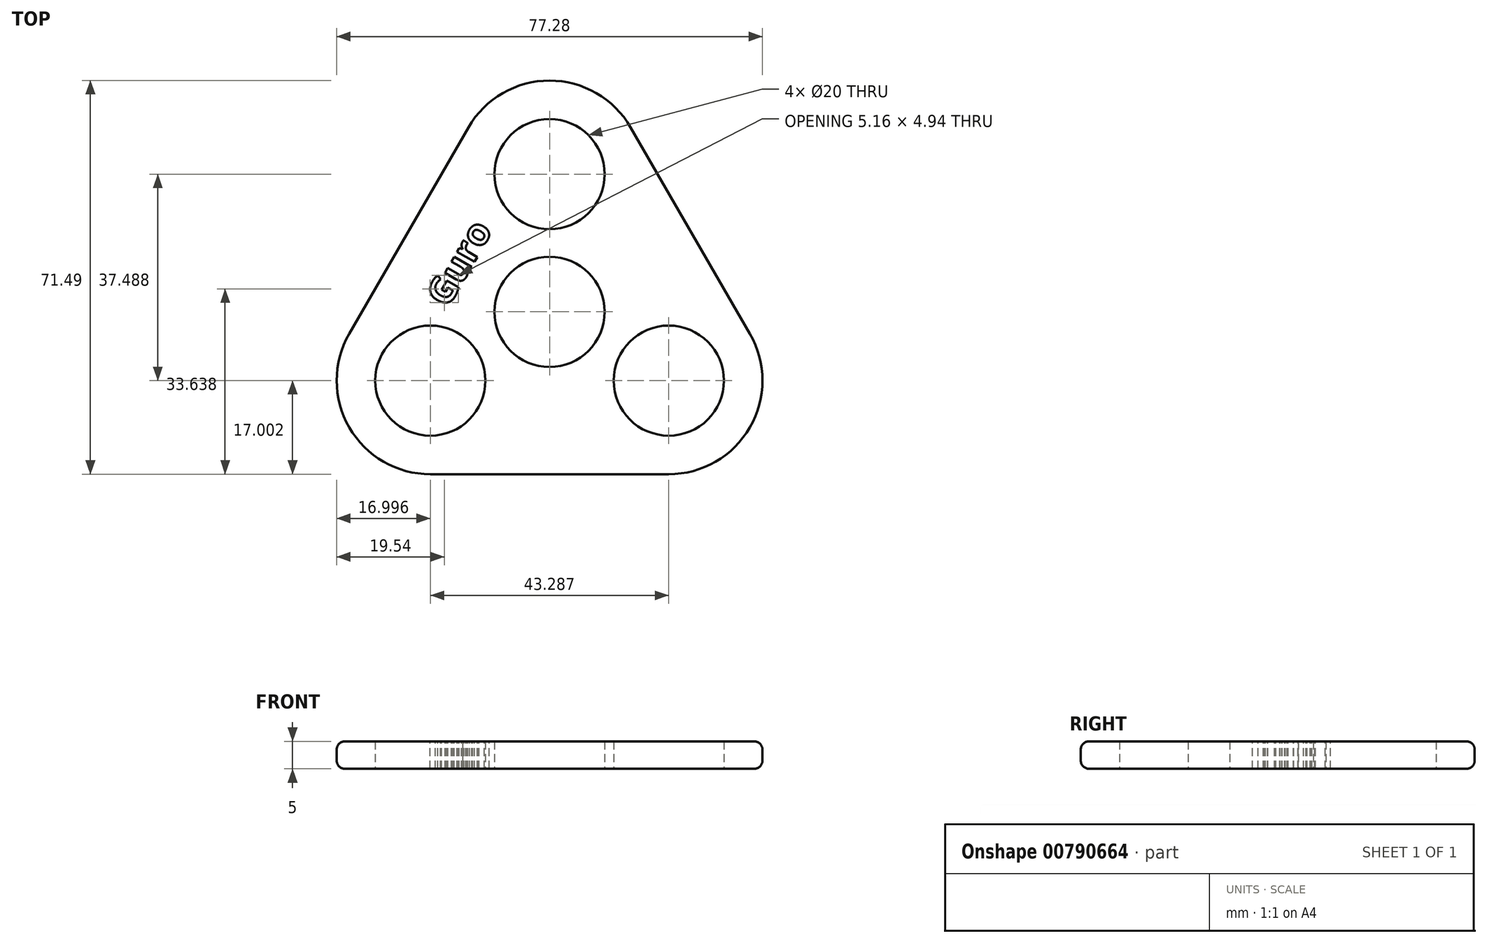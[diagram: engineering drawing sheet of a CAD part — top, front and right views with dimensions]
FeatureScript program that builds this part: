
annotation { "Feature Type Name" : "Feature", "Feature Type Description" : "" }
export const myFeature = defineFeature(function(context is Context, id is Id, definition is map)
    precondition{}
    {
        {
            var Q0;
            Q0=qCreatedBy(makeId("Top.planeOp"),FACE);
            var sketch = newSketch(context, id + "F0", { "sketchPlane" : qUnion([Q0])});
            skCircle(sketch, "E0", {"center": v(0, 0) * mm, "radius": 10 * mm});
            skCircle(sketch, "E1.0.1.0", {"center": v(0, 25) * mm, "radius": 10 * mm});
            skLineSegment(sketch, "E1.direction1", {"start": v(0, 0) * mm, "end": v(25, 0) * mm, "construction": true});
            skLineSegment(sketch, "E1.direction2", {"start": v(0, 0) * mm, "end": v(0, 25) * mm, "construction": true});
            skCircle(sketch, "E2.1.0", {"center": v(-21.64, -12.49) * mm, "radius": 10 * mm});
            skCircle(sketch, "E2.2.0", {"center": v(21.64, -12.49) * mm, "radius": 10 * mm});
            skArc(sketch, "E3.0", {"start": v(10.1, 0) * mm, "mid": v(10.05, -0.05) * mm, "end": v(10, -0.1) * mm});
            skArc(sketch, "E4.0", {"start": v(14.72, 33.5) * mm, "mid": v(0, 42) * mm, "end": v(-14.72, 33.5) * mm});
            skArc(sketch, "E5.0", {"start": v(-36.37, -3.99) * mm, "mid": v(-36.37, -20.99) * mm, "end": v(-21.64, -29.49) * mm});
            skLineSegment(sketch, "E6", {"start": v(-14.72, 33.5) * mm, "end": v(-36.37, -3.99) * mm});
            skLineSegment(sketch, "E7", {"start": v(-21.64, -29.49) * mm, "end": v(21.64, -29.49) * mm});
            skLineSegment(sketch, "E8", {"start": v(14.72, 33.5) * mm, "end": v(36.37, -3.99) * mm});
            skArc(sketch, "E9.trimOffspring", {"start": v(21.64, -29.49) * mm, "mid": v(36.37, -20.99) * mm, "end": v(36.37, -3.99) * mm});
            skSolve(sketch);
        }
        {
            var Q0;
            Q0=makeQuery(id+"F0.imprint","IMPRINT",FACE,{"disambiguationData":[TD([[makeQuery(id+"F0.imprint","IMPRINT",EDGE,{"derivedFrom":sQuery(id+"F0.wireOp",EDGE,"E0")}),-1.0]])]});
            extrude(context, id + "F1", {"entities" : qUnion([Q0]), "depth" : 5 * mm, "offsetDistance" : 25 * mm});
        }
        {
            var Q0;
            Q0=makeQuery(id+"F1.opExtrude","CAP_FACE",FACE,{"disambiguationData":[OSD([sQuery(id+"F0.wireOp",EDGE,"E0"),sQuery(id+"F0.wireOp",EDGE,"E1.0.1.0"),sQuery(id+"F0.wireOp",EDGE,"E2.1.0"),sQuery(id+"F0.wireOp",EDGE,"E2.2.0"),sQuery(id+"F0.wireOp",EDGE,"E4.0"),sQuery(id+"F0.wireOp",EDGE,"E5.0"),sQuery(id+"F0.wireOp",EDGE,"E6"),sQuery(id+"F0.wireOp",EDGE,"E7"),sQuery(id+"F0.wireOp",EDGE,"E8"),sQuery(id+"F0.wireOp",EDGE,"E9.trimOffspring")])],"isStart":false});
            var sketch = newSketch(context, id + "F2", { "sketchPlane" : qUnion([Q0])});
            skText(sketch, "E10", { "text": "Guro", "fontName": "OpenSans-Bold.ttf"});
            const initialGuessF2  = {"E10": [-0.0185, 0.0006, 0.5, 0.86603, 0.00483]};
            skSetInitialGuess(sketch, initialGuessF2);
            skSolve(sketch);
        }
        {
            var Q0;
            Q0 = qSketchRegion(id + "F2", true);
            extrude(context, id + "F3", {"entities" : qUnion([Q0]), "operationType" : NewBodyOperationType.REMOVE, "endBound" : BoundingType.THROUGH_ALL, "oppositeDirection" : true, "depth" : 25 * mm, "offsetDistance" : 25 * mm});
        }
        {
            var Q0;
            Q0=makeQuery(id+"F1.opExtrude","CAP_EDGE",EDGE,{"disambiguationData":[OSD([sQuery(id+"F0.wireOp",EDGE,"E6")])],"isStart":false});
            var Q1;
            Q1=makeQuery(id+"F1.opExtrude","CAP_EDGE",EDGE,{"disambiguationData":[OSD([sQuery(id+"F0.wireOp",EDGE,"E7")])],"isStart":true});
            var Q2;
            Q2=makeQuery(id+"F1.opExtrude","CAP_EDGE",EDGE,{"disambiguationData":[OSD([sQuery(id+"F0.wireOp",EDGE,"E5.0")])],"isStart":true});
            fillet(context, id + "F4", {"entities" : qUnion([Q0, Q1, Q2]), "radius" : 1.5 * mm, "tangentPropagation" : true, "allowEdgeOverflow" : false});
        }
    });
